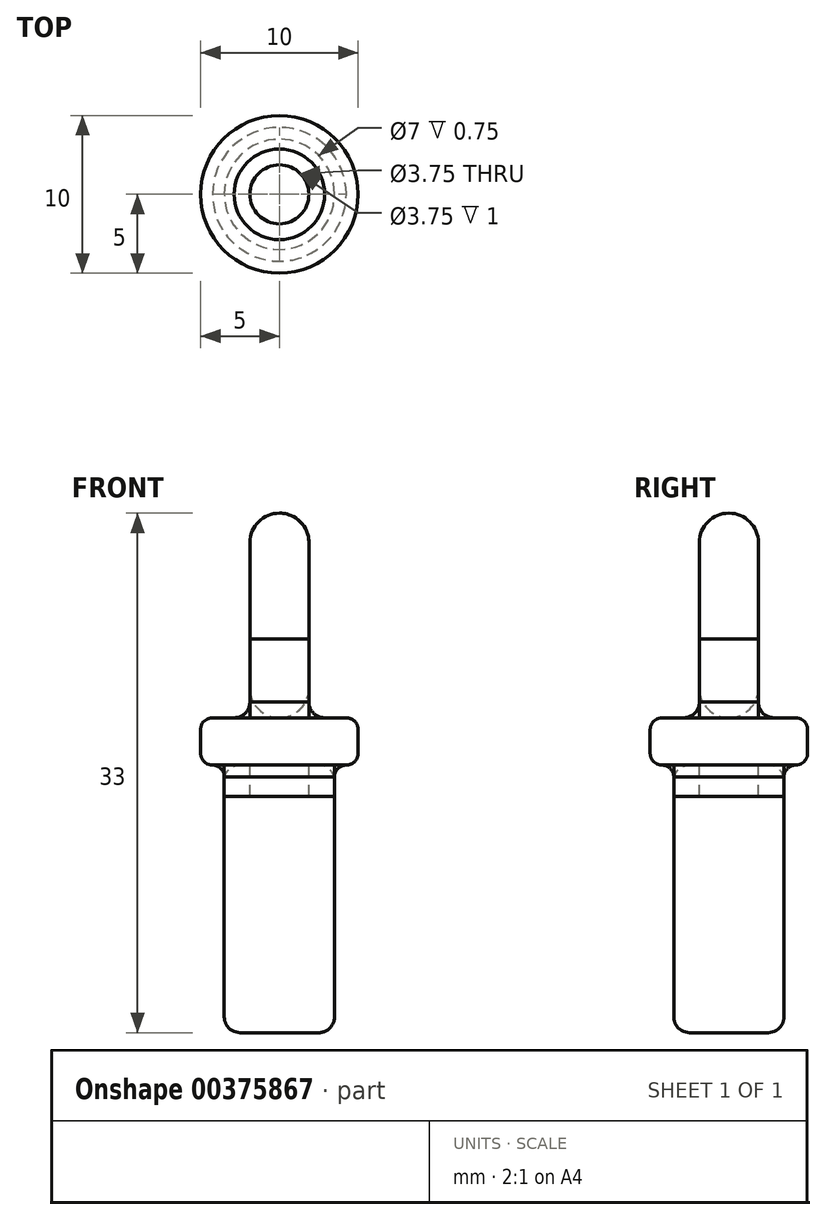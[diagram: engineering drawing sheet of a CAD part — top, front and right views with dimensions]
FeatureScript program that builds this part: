
annotation { "Feature Type Name" : "Feature", "Feature Type Description" : "" }
export const myFeature = defineFeature(function(context is Context, id is Id, definition is map)
    precondition{}
    {
        {
            var Q0;
            Q0=qCreatedBy(makeId("Top.planeOp"),FACE);
            var sketch = newSketch(context, id + "F0", { "sketchPlane" : qUnion([Q0])});
            skCircle(sketch, "E0", {"center": v(0, 0) * mm, "radius": 1.88 * mm});
            skCircle(sketch, "E1", {"center": v(0, 0) * mm, "radius": 3.5 * mm});
            skCircle(sketch, "E2", {"center": v(0, 0) * mm, "radius": 5 * mm});
            skSolve(sketch);
        }
        {
            var Q0;
            Q0=makeQuery(id+"F0.imprint","IMPRINT",FACE,{"disambiguationData":[TD([[makeQuery(id+"F0.imprint","IMPRINT",EDGE,{"derivedFrom":sQuery(id+"F0.wireOp",EDGE,"E0")}),1.0]])]});
            extrude(context, id + "F1", {"entities" : qUnion([Q0]), "depth" : 13 * mm});
        }
        {
            var Q0;
            Q0=makeQuery(id+"F0.imprint","IMPRINT",FACE,{"disambiguationData":[TD([[makeQuery(id+"F0.imprint","IMPRINT",EDGE,{"derivedFrom":sQuery(id+"F0.wireOp",EDGE,"E0")}),1.0]])]});
            var Q1;
            Q1=makeQuery(id+"F0.imprint","IMPRINT",FACE,{"disambiguationData":[TD([[makeQuery(id+"F0.imprint","IMPRINT",EDGE,{"derivedFrom":sQuery(id+"F0.wireOp",EDGE,"E0")}),-1.0]])]});
            extrude(context, id + "F2", {"entities" : qUnion([Q0, Q1]), "operationType" : NewBodyOperationType.ADD, "oppositeDirection" : true, "depth" : 20 * mm, "hasSecondDirection" : true, "secondDirectionOppositeDirection" : true, "secondDirectionDepth" : 3 * mm});
        }
        {
            var Q0;
            Q0=makeQuery(id+"F0.imprint","IMPRINT",FACE,{"disambiguationData":[TD([[makeQuery(id+"F0.imprint","IMPRINT",EDGE,{"derivedFrom":sQuery(id+"F0.wireOp",EDGE,"E0")}),1.0]])]});
            var Q1;
            Q1=makeQuery(id+"F0.imprint","IMPRINT",FACE,{"disambiguationData":[TD([[makeQuery(id+"F0.imprint","IMPRINT",EDGE,{"derivedFrom":sQuery(id+"F0.wireOp",EDGE,"E0")}),-1.0]])]});
            var Q2;
            Q2=makeQuery(id+"F0.imprint","IMPRINT",FACE,{"disambiguationData":[TD([[makeQuery(id+"F0.imprint","IMPRINT",EDGE,{"derivedFrom":sQuery(id+"F0.wireOp",EDGE,"E1")}),-1.0]])]});
            extrude(context, id + "F3", {"entities" : qUnion([Q0, Q1, Q2]), "oppositeDirection" : true, "depth" : 3 * mm});
        }
        {
            var Q0;
            Q0=makeQuery(id+"F1.opExtrude","SWEPT_FACE",FACE,{"disambiguationData":[OSD([sQuery(id+"F0.wireOp",EDGE,"E0")])]});
            var Q1;
            Q1=makeQuery(id+"F1.opExtrude","CAP_FACE",FACE,{"disambiguationData":[OSD([sQuery(id+"F0.wireOp",EDGE,"E0")])],"isStart":false});
            fillet(context, id + "F4", {"entities" : qUnion([Q0, Q1]), "radius" : 1.88 * mm, "allowEdgeOverflow" : false});
        }
        {
            var Q0;
            Q0=makeQuery(id+"F0.imprint","IMPRINT",FACE,{"disambiguationData":[TD([[makeQuery(id+"F0.imprint","IMPRINT",EDGE,{"derivedFrom":sQuery(id+"F0.wireOp",EDGE,"E0")}),1.0]])]});
            extrude(context, id + "F5", {"entities" : qUnion([Q0]), "depth" : 5 * mm});
        }
        {
            var Q0;
            Q0=qCreatedBy(makeId("Front.planeOp"),FACE);
            var sketch = newSketch(context, id + "F6", { "sketchPlane" : qUnion([Q0])});
            skCircle(sketch, "E3", {"center": v(-2.88, 1) * mm, "radius": 1 * mm});
            skLineSegment(sketch, "E4.bottom", {"start": v(-2.88, 1) * mm, "end": v(-1.88, 1) * mm});
            skLineSegment(sketch, "E4.top", {"start": v(-2.88, 0) * mm, "end": v(-1.88, 0) * mm});
            skLineSegment(sketch, "E4.left", {"start": v(-2.88, 1) * mm, "end": v(-2.88, 0) * mm});
            skLineSegment(sketch, "E4.right", {"start": v(-1.88, 1) * mm, "end": v(-1.88, 0) * mm});
            skSolve(sketch);
        }
        {
            var Q0;
            {var subQ2=sQuery(id+"F6.wireOp",EDGE,"E4.top");Q0=makeQuery(id+"F6.imprint","IMPRINT",FACE,{"disambiguationData":[TD([[makeQuery(id+"F6.imprint","IMPRINT",EDGE,{"derivedFrom":subQ2}),1.0]])]});}
            var Q1;
            Q1=makeQuery(id+"F5.opExtrude","SWEPT_FACE",FACE,{"disambiguationData":[OSD([sQuery(id+"F0.wireOp",EDGE,"E0")])]});
            revolve(context, id + "F7", {"entities" : qUnion([Q0]), "axis" : qUnion([Q1]), "revolveType" : RevolveType.FULL});
        }
        {
            var Q0;
            Q0=makeQuery(id+"F3.opExtrude","SWEPT_FACE",FACE,{"disambiguationData":[OSD([sQuery(id+"F0.wireOp",EDGE,"E2")])]});
            var Q1;
            Q1=makeQuery(id+"F3.opExtrude","CAP_FACE",FACE,{"disambiguationData":[OSD([sQuery(id+"F0.wireOp",EDGE,"E2")])],"isStart":true});
            fillet(context, id + "F8", {"entities" : qUnion([Q0, Q1]), "radius" : .75 * mm, "tangentPropagation" : true, "allowEdgeOverflow" : false});
        }
        {
            var Q0;
            Q0=makeQuery(id+"F2.opExtrude","SWEPT_FACE",FACE,{"disambiguationData":[OSD([sQuery(id+"F0.wireOp",EDGE,"E1")])]});
            var Q1;
            Q1=makeQuery(id+"F2.opExtrude","CAP_FACE",FACE,{"disambiguationData":[OSD([sQuery(id+"F0.wireOp",EDGE,"E1")])],"isStart":false});
            fillet(context, id + "F9", {"entities" : qUnion([Q0, Q1]), "radius" : 1 * mm, "tangentPropagation" : true, "allowEdgeOverflow" : false});
        }
        {
            var Q0;
            Q0=makeQuery(id+"F0.imprint","IMPRINT",FACE,{"disambiguationData":[TD([[makeQuery(id+"F0.imprint","IMPRINT",EDGE,{"derivedFrom":sQuery(id+"F0.wireOp",EDGE,"E0")}),-1.0]])]});
            extrude(context, id + "F10", {"entities" : qUnion([Q0]), "oppositeDirection" : true, "depth" : 5 * mm, "hasSecondDirection" : true, "secondDirectionOppositeDirection" : true, "secondDirectionDepth" : 3 * mm});
        }
        {
            var Q0;
            Q0=qCreatedBy(makeId("Front.planeOp"),FACE);
            var sketch = newSketch(context, id + "F11", { "sketchPlane" : qUnion([Q0])});
            skCircle(sketch, "E5", {"center": v(4.25, -3.75) * mm, "radius": 0.75 * mm});
            skLineSegment(sketch, "E6.bottom", {"start": v(4.25, -3.75) * mm, "end": v(3.5, -3.75) * mm});
            skLineSegment(sketch, "E6.top", {"start": v(4.25, -3) * mm, "end": v(3.5, -3) * mm});
            skLineSegment(sketch, "E6.left", {"start": v(4.25, -3.75) * mm, "end": v(4.25, -3) * mm});
            skLineSegment(sketch, "E6.right", {"start": v(3.5, -3.75) * mm, "end": v(3.5, -3) * mm});
            skSolve(sketch);
        }
        {
            var Q0;
            {var subQ2=sQuery(id+"F11.wireOp",EDGE,"E6.top");Q0=makeQuery(id+"F11.imprint","IMPRINT",FACE,{"disambiguationData":[TD([[makeQuery(id+"F11.imprint","IMPRINT",EDGE,{"derivedFrom":subQ2}),1.0]])]});}
            var Q1;
            Q1=makeQuery(id+"F10.opExtrude","SWEPT_FACE",FACE,{"disambiguationData":[OSD([sQuery(id+"F0.wireOp",EDGE,"E1")])]});
            revolve(context, id + "F12", {"entities" : qUnion([Q0]), "axis" : qUnion([Q1]), "revolveType" : RevolveType.FULL});
        }
    });
